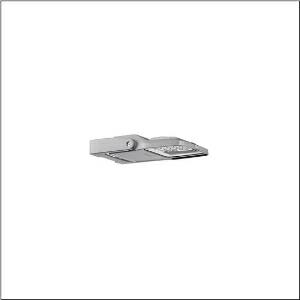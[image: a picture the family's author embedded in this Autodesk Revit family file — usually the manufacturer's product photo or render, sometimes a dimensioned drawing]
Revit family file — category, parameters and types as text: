
# Revit family: floodlight_fl_21_iq_micro___pl52_5xa7761a4d2a_29c7
name_source: partatom
category: Lighting Fixtures
units: mm (PartAtom-declared; Revit-internal decimal feet)

## family parameters
Cut with Voids When Loaded = No
Host = Face
Light Source = No
Part Type = Normal
Room Calculation Point = No
Round Connector Dimension = Use Diameter
Shared = No

## types (1)
- --- (1 x LED, 3010 lm, 23.1 W, 4000K)
    Apparent Load = 23 VA
    CIE Flux Codes = 26 60 98 100 100
    Color Rendering = 70
    Color Temperature = 4000K
    Default Elevation = 1800 mm
    Description = Floodlight FL 21 iQ micro, floodlight, primary light control with lens, of PMMA, primary optical cover: protective disc, of toughened safety glass, transparent, light distribution: PL52, light emission: direct distribution, installation type: surface-mounted, lamps: LED, High Power LED, rated values: 3.010lm | 23,1W | 130,3lm/W (begin service life); end service life: 3.010lm | 23,8W; at 50% lumin. flux: 1.505lm | 11W | 136,8lm/W, colour temperature: 4000K, colour rendering: CRI > 70, light colour: 740, light setting 1 begin service life: 100% | 3.010lm | 23,1W | 130,3lm/W | 4.000K, light setting 1 end service life: 23,8W, further light settings possible, control: optimised constant luminous flux control (CLO 2.0), Desk-Remote (wireless, voltage-free reading and setting of iQ features in the workshop via application-optimized NFC function/RFID function), Light-Fading, Smart-Wire, Night-Set, Lumen-Switch, Temp-Guard, Auto-Match, pre-setting: linear dimming characteristic, with terminal, 6-pole, mains connection: 220..240V, AC, 50/60Hz, luminaire housing, of diecast aluminium, powder-coated, SITECO metallic grey (DB 702S), corrosivity category C5 mid according to DIN EN ISO 12944suitable for swimming poolschlorine-resistant, sealing non-destructively replaceable, design bracket, of diecast aluminium, powder-coated, SITECO metallic grey (DB 702S), protection rating (complete): IP66, insulation class (complete): insulation class II (safety insulation), certification: CE, ENEC, VDE, protection symbol: D, impact resistance: IK07, permissible operating ambient temperature: -40..+40°C, permissible operating ambient temperature for outdoor applications: -40..+50°C, standard: DIN EN 12944, LABS conformity tested according to VDMA 24364:2018-05, packaging unit: 1 piece

Light Distribution: PL52
    Height = 65 mm
    Lamp = 1 x LED
    Lamp Light Flux = 3010 lm
    Lamp Power = 23.1 W
    Lamp count = 1
    Length = 312 mm
    Luminous efficacy = 130 lm/W
    Manufacturer = Siteco
    ModVariant = No
    Model = 5XA7761A4D2A
    Mounting Place = Wall
    Mounting Type = Surface mounted
    Number of Poles = 1
    OnlyDefault = Yes
    Power Factor = 1
    Product Name = Floodlight FL 21 iQ micro | PL52
    Product group = floodlight | wall mounted
    ProductGroupID = 2002
    Protection Class = Protection class II
    Protection Degree = IP 66
    RLX_Detail_Level = 1
    RLX_Emergency_Light_Flux = 0 lm
    RLX_Emergency_Type = 0
    RLX_Emergency_Type_DB = No
    RlxData = <blob elided: 97853 chars, md5=7d2c4cbc>
    Socket = socket
    Standby Power = 0 W
    System Light Flux = 3010 lm
    System Power = 23 W
    Type Comments = factory setting: luminous flux: 100 % | dim-lin: 254 | 455 mA
    Type Image = l_1006878.jpg
    URL = http://relux.com
    VarID = @adj_177507
    Voltage = 0 V
    Weight = 0.00 kg
    Width = 230 mm

## geometry (parser evidence)
native form markers: Blend x4, Sweep x12
no freeform markers — native parametric forms only
